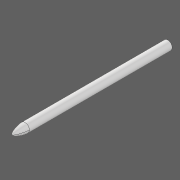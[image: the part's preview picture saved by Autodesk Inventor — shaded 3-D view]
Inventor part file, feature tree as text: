
AUTODESK INVENTOR PART (.ipt)
format: ipt  version: 2020 (Build 240168000, 168)  size: 90,624 bytes
history: native  units: in
note: dims shown in document units (in); Inventor stores cm internally (conversion verified against a paired STEP export)
features: revolve x1, sketch x1
ambient origin geometry x8: Origin, YZ Plane, XZ Plane, XY Plane, X Axis, Y Axis, Z Axis, Center Point
bodies: Solid1 (feature_tree)
feature tree (2):
  revolve  "Revolution1"  [1 undecoded]
  sketch  "Sketch1"  dims[d0=90.0deg d1=0.1969in d2=0.5906in d3=0.1969in d4=0.0787in d5=7.0866in]
note: 1 required parameter value undecoded (feature->parameter linkage not recoverable at this tier; creation-order binding heuristic only, values carry confidence <= 0.55)
